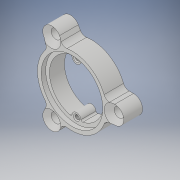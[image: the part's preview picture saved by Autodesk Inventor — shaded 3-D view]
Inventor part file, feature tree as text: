
AUTODESK INVENTOR PART (.ipt)
format: ipt  version: 2019.4 (Build 234330000, 330)  size: 218,112 bytes
history: native  units: mm
features: sketch x6, extrude x4, pattern_circular x2, hole x2, fillet x2, chamfer x1
ambient origin geometry x8: Origin, YZ Plane, XZ Plane, XY Plane, X Axis, Y Axis, Z Axis, Center Point
bodies: Solid1 (feature_tree)
feature tree (17):
  extrude  "Extrusion1"  Depth=5.0mm TaperAngle=0.0deg
  extrude  "Extrusion2"  Depth=20.5mm
  extrude  "Extrusion4"  Depth=14.0mm
  pattern_circular  "Circular Pattern1"  Count=3 Angle=360.0deg
  hole  "Hole1"  [1 undecoded]
  pattern_circular  "Circular Pattern2"  [2 undecoded]
  fillet  "Fillet1"  Radius=17.0mm
  extrude  "Extrusion5"  Depth=3.0mm
  hole  "Hole2"  [1 undecoded]
  fillet  "Fillet2"  Radius=1.0mm
  chamfer  "Chamfer1"  Distance=0.5mm
  sketch  "Sketch1"  dims[d1=18.0mm d2=5.0mm d3=0.0mm]
  sketch  "Sketch2"  dims[d4=23.0mm d5=20.5mm]
  sketch  "Sketch4"  dims[d6=1.5mm d7=0.0mm d13=14.0mm]
  sketch  "Sketch5"  dims[d14=6.0mm]
  sketch  "Sketch6"  dims[d15=1.0mm d16=0.0mm d17=30.0mm d18=360.0deg]
  sketch  "Sketch7"  dims[d20=3.0mm d21=3.2mm d22=6.0mm d23=6.5mm d24=2.0mm d25=90.0deg d26=15.0mm d27=0.0mm d28=30.0mm d29=360.0deg d31=2.0mm d32=17.0mm d33=3.0mm d34=3.0mm d35=1.0mm d36=0.0mm d37=1.421mm d38=6.0mm d39=6.5mm d40=2.0mm d41=90.0deg d42=7.0mm d43=0.0mm d44=0.5mm d45=0.3mm d46=2.0mm d47=45.0deg]
note: 4 required parameter values undecoded (feature->parameter linkage not recoverable at this tier; creation-order binding heuristic only, values carry confidence <= 0.55)
